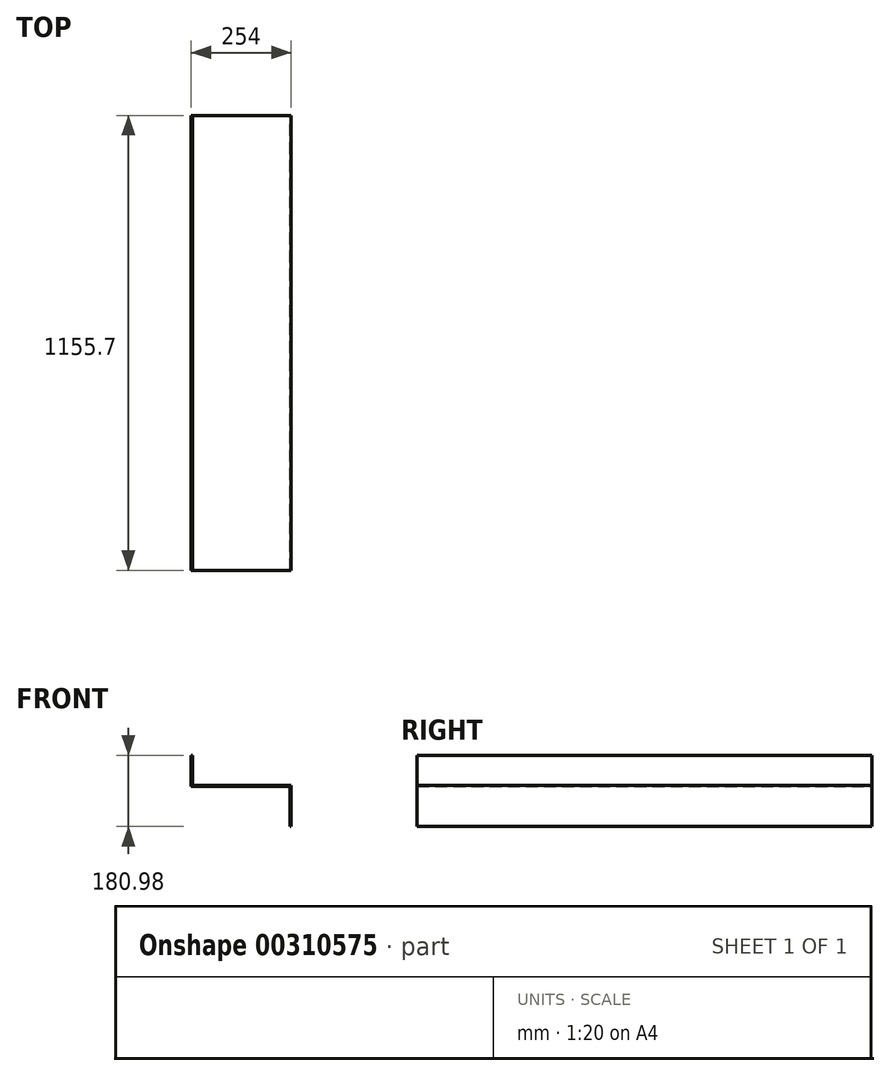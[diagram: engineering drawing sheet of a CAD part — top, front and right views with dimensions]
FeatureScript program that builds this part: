
annotation { "Feature Type Name" : "Feature", "Feature Type Description" : "" }
export const myFeature = defineFeature(function(context is Context, id is Id, definition is map)
    precondition{}
    {
        {
            var Q0;
            Q0=qCreatedBy(makeId("Top.planeOp"),FACE);
            var sketch = newSketch(context, id + "F0", { "sketchPlane" : qUnion([Q0])});
            skLineSegment(sketch, "E0.bottom", {"start": v(0, 0) * mm, "end": v(254, 0) * mm});
            skLineSegment(sketch, "E0.top", {"start": v(0, 1155.7) * mm, "end": v(254, 1155.7) * mm});
            skLineSegment(sketch, "E0.left", {"start": v(0, 0) * mm, "end": v(0, 1155.7) * mm});
            skLineSegment(sketch, "E0.right", {"start": v(254, 0) * mm, "end": v(254, 1155.7) * mm});
            skSolve(sketch);
        }
        {
            var Q0;
            Q0 = qSketchRegion(id + "F0", true);
            extrude(context, id + "F1", {"entities" : qUnion([Q0]), "depth" : 3.17 * mm});
        }
        {
            var Q0;
            Q0=makeQuery(id+"F1.opExtrude","CAP_FACE",FACE,{"disambiguationData":[OSD([sQuery(id+"F0.wireOp",EDGE,"E0.bottom"),sQuery(id+"F0.wireOp",EDGE,"E0.top"),sQuery(id+"F0.wireOp",EDGE,"E0.left"),sQuery(id+"F0.wireOp",EDGE,"E0.right")])],"isStart":false});
            var sketch = newSketch(context, id + "F2", { "sketchPlane" : qUnion([Q0])});
            skLineSegment(sketch, "E1", {"start": v(3.18, 0) * mm, "end": v(3.17, 1155.7) * mm});
            skLineSegment(sketch, "E2", {"start": v(3.17, 1155.7) * mm, "end": v(0, 1155.7) * mm});
            skLineSegment(sketch, "E3", {"start": v(0, 1155.7) * mm, "end": v(0, 0) * mm});
            skLineSegment(sketch, "E4", {"start": v(0, 0) * mm, "end": v(3.18, 0) * mm});
            skSolve(sketch);
        }
        {
            var Q0;
            Q0=makeQuery(id+"F2.imprint","IMPRINT",FACE,{"disambiguationData":[TD([[makeQuery(id+"F2.imprint","IMPRINT",EDGE,{"derivedFrom":sQuery(id+"F2.wireOp",EDGE,"E1")}),1.0]])]});
            extrude(context, id + "F3", {"entities" : qUnion([Q0]), "operationType" : NewBodyOperationType.ADD, "depth" : 76.2 * mm});
        }
        {
            var Q0;
            Q0=makeQuery(id+"F1.opExtrude","CAP_FACE",FACE,{"disambiguationData":[OSD([sQuery(id+"F0.wireOp",EDGE,"E0.bottom"),sQuery(id+"F0.wireOp",EDGE,"E0.top"),sQuery(id+"F0.wireOp",EDGE,"E0.left"),sQuery(id+"F0.wireOp",EDGE,"E0.right")])],"isStart":true});
            var sketch = newSketch(context, id + "F4", { "sketchPlane" : qUnion([Q0])});
            skLineSegment(sketch, "E5.bottom", {"start": v(254, 0) * mm, "end": v(250.82, 0) * mm});
            skLineSegment(sketch, "E5.top", {"start": v(254, -1155.7) * mm, "end": v(250.83, -1155.7) * mm});
            skLineSegment(sketch, "E5.left", {"start": v(254, 0) * mm, "end": v(254, -1155.7) * mm});
            skLineSegment(sketch, "E5.right", {"start": v(250.82, 0) * mm, "end": v(250.83, -1155.7) * mm});
            skSolve(sketch);
        }
        {
            var Q0;
            Q0=makeQuery(id+"F4.imprint","IMPRINT",FACE,{"disambiguationData":[TD([[makeQuery(id+"F4.imprint","IMPRINT",EDGE,{"derivedFrom":sQuery(id+"F4.wireOp",EDGE,"E5.bottom")}),-1.0]])]});
            extrude(context, id + "F5", {"entities" : qUnion([Q0]), "operationType" : NewBodyOperationType.ADD, "depth" : 101.6 * mm});
        }
    });
